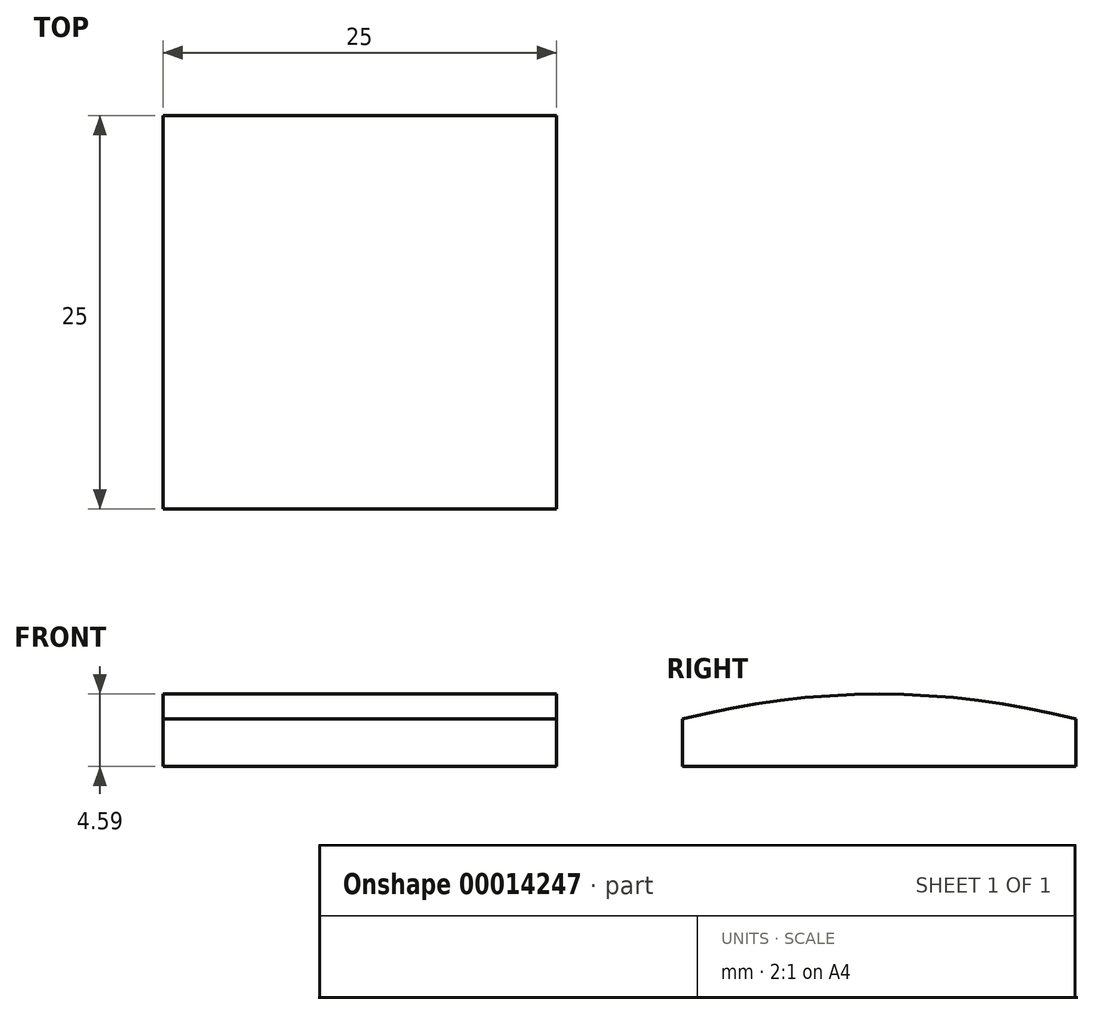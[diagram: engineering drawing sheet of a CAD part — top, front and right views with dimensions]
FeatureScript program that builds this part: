
annotation { "Feature Type Name" : "Feature", "Feature Type Description" : "" }
export const myFeature = defineFeature(function(context is Context, id is Id, definition is map)
    precondition{}
    {
        {
            var Q0;
            Q0=qCreatedBy(makeId("Right.planeOp"),FACE);
            var sketch = newSketch(context, id + "F0", { "sketchPlane" : qUnion([Q0])});
            skLineSegment(sketch, "E0", {"start": v(0, 0) * mm, "end": v(12.5, 0) * mm});
            skLineSegment(sketch, "E1", {"start": v(12.5, 0) * mm, "end": v(12.5, 3) * mm});
            skLineSegment(sketch, "E2", {"start": v(0, 19.22) * mm, "end": v(0, -21.05) * mm, "construction": true});
            skLineSegment(sketch, "E3.MirrorCS", {"start": v(0, 0) * mm, "end": v(-12.5, 0) * mm});
            skLineSegment(sketch, "E4.MirrorCS", {"start": v(-12.5, 0) * mm, "end": v(-12.5, 3) * mm});
            skArc(sketch, "E5", {"start": v(12.5, 3) * mm, "mid": v(0, 4.59) * mm, "end": v(-12.5, 3) * mm});
            skSolve(sketch);
        }
        {
            var Q0;
            Q0=makeQuery(id+"F0.imprint","IMPRINT",FACE,{"disambiguationData":[TD([[makeQuery(id+"F0.imprint","IMPRINT",EDGE,{"derivedFrom":sQuery(id+"F0.wireOp",EDGE,"E0")}),1.0]])]});
            extrude(context, id + "F1", {"entities" : qUnion([Q0]), "endBound" : BoundingType.SYMMETRIC, "depth" : 25 * mm});
        }
    });
